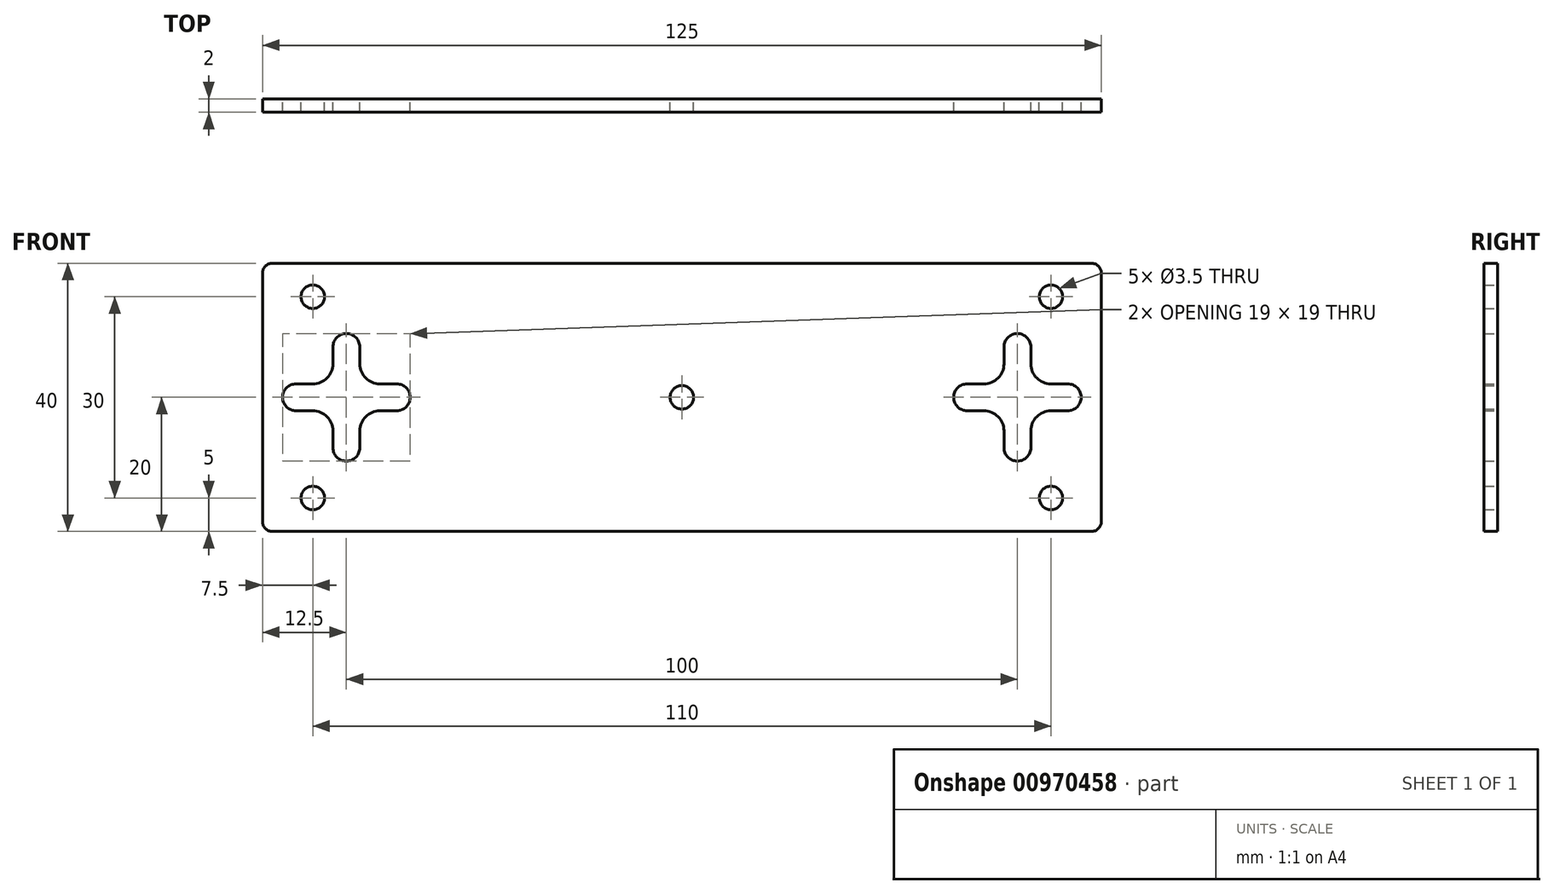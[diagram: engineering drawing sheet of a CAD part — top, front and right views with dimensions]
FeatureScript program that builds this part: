
annotation { "Feature Type Name" : "Feature", "Feature Type Description" : "" }
export const myFeature = defineFeature(function(context is Context, id is Id, definition is map)
    precondition{}
    {
        {
            var Q0;
            Q0=qCreatedBy(makeId("Front.planeOp"),FACE);
            var sketch = newSketch(context, id + "F0", { "sketchPlane" : qUnion([Q0])});
            skLineSegment(sketch, "E0.0", {"start": v(-62.5, 20) * mm, "end": v(62.5, 20) * mm});
            skLineSegment(sketch, "E1.0", {"start": v(-62.5, -20) * mm, "end": v(-62.5, 20) * mm});
            skLineSegment(sketch, "E2.0", {"start": v(-62.5, -20) * mm, "end": v(62.5, -20) * mm});
            skLineSegment(sketch, "E3.0", {"start": v(62.5, -20) * mm, "end": v(62.5, 20) * mm});
            skLineSegment(sketch, "E4.filletArc", {"start": v(-62.5, 20) * mm, "end": v(-62.5, 20) * mm});
            skLineSegment(sketch, "E5.filletArc", {"start": v(-62.5, -20) * mm, "end": v(-62.5, -20) * mm});
            skLineSegment(sketch, "E6.filletArc", {"start": v(62.5, -20) * mm, "end": v(62.5, -20) * mm});
            skLineSegment(sketch, "E7.filletArc", {"start": v(62.5, 20) * mm, "end": v(62.5, 20) * mm});
            skCircle(sketch, "E8", {"center": v(-55, 15) * mm, "radius": 1.75 * mm});
            skCircle(sketch, "E9", {"center": v(55, 15) * mm, "radius": 1.75 * mm});
            skCircle(sketch, "E10", {"center": v(-55, -15) * mm, "radius": 1.75 * mm});
            skCircle(sketch, "E11", {"center": v(55, -15) * mm, "radius": 1.75 * mm});
            skLineSegment(sketch, "E12", {"start": v(-50, 7.5) * mm, "end": v(-50, -7.5) * mm});
            skLineSegment(sketch, "E13", {"start": v(42.5, 0) * mm, "end": v(57.5, 0) * mm});
            skLineSegment(sketch, "E14", {"start": v(50, 7.5) * mm, "end": v(50, -7.5) * mm});
            skLineSegment(sketch, "E15", {"start": v(-57.5, 0) * mm, "end": v(-42.5, 0) * mm});
            skArc(sketch, "E16.0.startCap", {"start": v(48, 7.5) * mm, "mid": v(50, 9.5) * mm, "end": v(52, 7.5) * mm});
            skArc(sketch, "E16.0.endCap", {"start": v(52, -7.5) * mm, "mid": v(50, -9.5) * mm, "end": v(48, -7.5) * mm});
            skLineSegment(sketch, "E16.0.left", {"start": v(52, 7.5) * mm, "end": v(52, -7.5) * mm});
            skLineSegment(sketch, "E16.0.right", {"start": v(48, 7.5) * mm, "end": v(48, -7.5) * mm});
            skArc(sketch, "E17.0.startCap", {"start": v(42.5, -2) * mm, "mid": v(40.5, 0) * mm, "end": v(42.5, 2) * mm});
            skArc(sketch, "E17.0.endCap", {"start": v(57.5, 2) * mm, "mid": v(59.5, 0) * mm, "end": v(57.5, -2) * mm});
            skLineSegment(sketch, "E17.0.left", {"start": v(42.5, 2) * mm, "end": v(57.5, 2) * mm});
            skLineSegment(sketch, "E17.0.right", {"start": v(42.5, -2) * mm, "end": v(57.5, -2) * mm});
            skArc(sketch, "E17.1.startCap", {"start": v(-57.5, -2) * mm, "mid": v(-59.5, 0) * mm, "end": v(-57.5, 2) * mm});
            skArc(sketch, "E17.1.endCap", {"start": v(-42.5, 2) * mm, "mid": v(-40.5, 0) * mm, "end": v(-42.5, -2) * mm});
            skLineSegment(sketch, "E17.1.left", {"start": v(-57.5, 2) * mm, "end": v(-42.5, 2) * mm});
            skLineSegment(sketch, "E17.1.right", {"start": v(-57.5, -2) * mm, "end": v(-42.5, -2) * mm});
            skArc(sketch, "E17.2.startCap", {"start": v(-52, 7.5) * mm, "mid": v(-50, 9.5) * mm, "end": v(-48, 7.5) * mm});
            skArc(sketch, "E17.2.endCap", {"start": v(-48, -7.5) * mm, "mid": v(-50, -9.5) * mm, "end": v(-52, -7.5) * mm});
            skLineSegment(sketch, "E17.2.left", {"start": v(-48, 7.5) * mm, "end": v(-48, -7.5) * mm});
            skLineSegment(sketch, "E17.2.right", {"start": v(-52, 7.5) * mm, "end": v(-52, -7.5) * mm});
            skCircle(sketch, "E18", {"center": v(0, 0) * mm, "radius": 1.75 * mm});
            skSolve(sketch);
        }
        {
            var Q0;
            {var subQ14=sQuery(id+"F0.wireOp",EDGE,"E0.0");Q0=makeQuery(id+"F0.imprint","IMPRINT",FACE,{"disambiguationData":[TD([[makeQuery(id+"F0.imprint","IMPRINT",EDGE,{"derivedFrom":subQ14}),-1.0]])]});}
            var Q1;
            {var subQ10=sQuery(id+"F0.wireOp",EDGE,"E2.0");Q1=makeQuery(id+"F0.imprint","IMPRINT",FACE,{"disambiguationData":[TD([[makeQuery(id+"F0.imprint","IMPRINT",EDGE,{"derivedFrom":subQ10}),1.0]])]});}
            var Q2;
            {var subQ1=sQuery(id+"F0.wireOp",EDGE,"X3yWnhJm-qIiu-0vvX-LXHK-jDvgxX4Z6LWV.bottom");var subQ3=sQuery(id+"F0.wireOp",EDGE,"iid6QfgW-px9S-WGrx-PAUP-FnRUA4cKeCWQ");var subQ4=makeQuery(id+"F0.imprint","INTERSECT",VERTEX,{"derivedFrom":[subQ1,subQ3]});Q2=makeQuery(id+"F0.imprint","IMPRINT",FACE,{"disambiguationData":[TD([[makeQuery(id+"F0.imprint","IMPRINT",EDGE,{"disambiguationData":[TD([[subQ4,-1.0]])],"derivedFrom":subQ3}),-1.0]])]});}
            var Q3;
            {var subQ5=sQuery(id+"F0.wireOp",EDGE,"E10");var subQ6=sQuery(id+"F0.wireOp",EDGE,"X3yWnhJm-qIiu-0vvX-LXHK-jDvgxX4Z6LWV.bottom");var subQ7=makeQuery(id+"F0.imprint","INTERSECT",VERTEX,{"derivedFrom":[subQ6,subQ5]});Q3=makeQuery(id+"F0.imprint","IMPRINT",FACE,{"disambiguationData":[TD([[makeQuery(id+"F0.imprint","IMPRINT",EDGE,{"disambiguationData":[TD([[subQ7,-1.0]])],"derivedFrom":subQ6}),1.0]])]});}
            var Q4;
            {var subQ1=sQuery(id+"F0.wireOp",EDGE,"X3yWnhJm-qIiu-0vvX-LXHK-jDvgxX4Z6LWV.top");var subQ11=sQuery(id+"F0.wireOp",EDGE,"iid6QfgW-px9S-WGrx-PAUP-FnRUA4cKeCWQ");var subQ12=makeQuery(id+"F0.imprint","INTERSECT",VERTEX,{"derivedFrom":[subQ1,subQ11]});Q4=makeQuery(id+"F0.imprint","IMPRINT",FACE,{"disambiguationData":[TD([[makeQuery(id+"F0.imprint","IMPRINT",EDGE,{"disambiguationData":[TD([[subQ12,-1.0]])],"derivedFrom":subQ1}),-1.0]])]});}
            var Q5;
            {var subQ1=sQuery(id+"F0.wireOp",EDGE,"X3yWnhJm-qIiu-0vvX-LXHK-jDvgxX4Z6LWV.top");var subQ3=sQuery(id+"F0.wireOp",EDGE,"iid6QfgW-px9S-WGrx-PAUP-FnRUA4cKeCWQ");var subQ4=makeQuery(id+"F0.imprint","INTERSECT",VERTEX,{"derivedFrom":[subQ1,subQ3]});Q5=makeQuery(id+"F0.imprint","IMPRINT",FACE,{"disambiguationData":[TD([[makeQuery(id+"F0.imprint","IMPRINT",EDGE,{"disambiguationData":[TD([[subQ4,1.0]])],"derivedFrom":subQ3}),1.0]])]});}
            var Q6;
            {var subQ0=sQuery(id+"F0.wireOp",EDGE,"i4QyBCOg-cULm-5afE-RLwa-3CR6AZ6ktZAw");Q6=makeQuery(id+"F0.imprint","IMPRINT",FACE,{"disambiguationData":[TD([[makeQuery(id+"F0.imprint","IMPRINT",EDGE,{"derivedFrom":subQ0}),1.0]])]});}
            var Q7;
            Q7=makeQuery(id+"F0.imprint","IMPRINT",FACE,{"disambiguationData":[TD([[makeQuery(id+"F0.imprint","IMPRINT",EDGE,{"derivedFrom":sQuery(id+"F0.wireOp",EDGE,"mcuOtgL4-kk58-VkkY-zE61-ACZWzzPfrjxR")}),-1.0]])]});
            var Q8;
            {var subQ0=sQuery(id+"F0.wireOp",EDGE,"KWtc0nGb-DVKQ-R7uK-HgXM-ysEQQWN5L63F");var subQ1=sQuery(id+"F0.wireOp",EDGE,"4OTX3qk5-V7Ov-Qq6L-etMf-vckOSsjvSIyS");var subQ2=makeQuery(id+"F0.imprint","INTERSECT",VERTEX,{"derivedFrom":[subQ1,subQ0]});Q8=makeQuery(id+"F0.imprint","IMPRINT",FACE,{"disambiguationData":[TD([[makeQuery(id+"F0.imprint","IMPRINT",EDGE,{"disambiguationData":[TD([[subQ2,-1.0]])],"derivedFrom":subQ1}),-1.0]])]});}
            var Q9;
            {var subQ1=sQuery(id+"F0.wireOp",EDGE,"4OTX3qk5-V7Ov-Qq6L-etMf-vckOSsjvSIyS");var subQ6=sQuery(id+"F0.wireOp",EDGE,"iid6QfgW-px9S-WGrx-PAUP-FnRUA4cKeCWQ");var subQ9=makeQuery(id+"F0.imprint","INTERSECT",VERTEX,{"disambiguationData":[OD(1.0)],"derivedFrom":[subQ6,subQ1]});Q9=makeQuery(id+"F0.imprint","IMPRINT",FACE,{"disambiguationData":[TD([[makeQuery(id+"F0.imprint","IMPRINT",EDGE,{"disambiguationData":[TD([[subQ9,-1.0]])],"derivedFrom":subQ6}),1.0]])]});}
            var Q10;
            {var subQ5=sQuery(id+"F0.wireOp",EDGE,"eCR2NoOr-Eci4-ocfl-Ev2O-bT8fmTrP9O9z");var subQ6=sQuery(id+"F0.wireOp",EDGE,"iid6QfgW-px9S-WGrx-PAUP-FnRUA4cKeCWQ");var subQ7=makeQuery(id+"F0.imprint","INTERSECT",VERTEX,{"disambiguationData":[OD(1.0)],"derivedFrom":[subQ6,subQ5]});Q10=makeQuery(id+"F0.imprint","IMPRINT",FACE,{"disambiguationData":[TD([[makeQuery(id+"F0.imprint","IMPRINT",EDGE,{"disambiguationData":[TD([[subQ7,-1.0]])],"derivedFrom":subQ6}),1.0]])]});}
            var Q11;
            {var subQ0=sQuery(id+"F0.wireOp",EDGE,"KsEaITvz-aWfB-0gTG-2vQc-Dy6UcmHyx8SA");var subQ5=sQuery(id+"F0.wireOp",EDGE,"Y71Hv5pT-VDeY-pl7A-gw0W-9l02TnNV8O4Y");var subQ6=makeQuery(id+"F0.imprint","INTERSECT",VERTEX,{"disambiguationData":[OD(0.0)],"derivedFrom":[subQ0,subQ5]});Q11=makeQuery(id+"F0.imprint","IMPRINT",FACE,{"disambiguationData":[TD([[makeQuery(id+"F0.imprint","IMPRINT",EDGE,{"disambiguationData":[TD([[subQ6,-1.0]])],"derivedFrom":subQ0}),-1.0]])]});}
            var Q12;
            {var subQ0=sQuery(id+"F0.wireOp",EDGE,"eCR2NoOr-Eci4-ocfl-Ev2O-bT8fmTrP9O9z");var subQ1=sQuery(id+"F0.wireOp",EDGE,"iAqB02pa-lLI2-8K0O-0Iya-2bA1iniOnDgh");var subQ2=makeQuery(id+"F0.imprint","INTERSECT",VERTEX,{"disambiguationData":[OD(0.0)],"derivedFrom":[subQ1,subQ0]});Q12=makeQuery(id+"F0.imprint","IMPRINT",FACE,{"disambiguationData":[TD([[makeQuery(id+"F0.imprint","IMPRINT",EDGE,{"disambiguationData":[TD([[subQ2,-1.0]])],"derivedFrom":subQ1}),-1.0]])]});}
            var Q13;
            {var subQ0=sQuery(id+"F0.wireOp",EDGE,"eCR2NoOr-Eci4-ocfl-Ev2O-bT8fmTrP9O9z");var subQ1=sQuery(id+"F0.wireOp",EDGE,"iAqB02pa-lLI2-8K0O-0Iya-2bA1iniOnDgh");var subQ2=makeQuery(id+"F0.imprint","INTERSECT",VERTEX,{"disambiguationData":[OD(0.0)],"derivedFrom":[subQ1,subQ0]});Q13=makeQuery(id+"F0.imprint","IMPRINT",FACE,{"disambiguationData":[TD([[makeQuery(id+"F0.imprint","IMPRINT",EDGE,{"disambiguationData":[TD([[subQ2,-1.0]])],"derivedFrom":subQ1}),1.0]])]});}
            var Q14;
            {var subQ1=sQuery(id+"F0.wireOp",EDGE,"iid6QfgW-px9S-WGrx-PAUP-FnRUA4cKeCWQ");var subQ6=sQuery(id+"F0.wireOp",EDGE,"xezjStJQ-Z63Z-E7xO-FFxy-wJp8TU6c4T7D");var subQ9=makeQuery(id+"F0.imprint","INTERSECT",VERTEX,{"disambiguationData":[OD(0.0)],"derivedFrom":[subQ1,subQ6]});Q14=makeQuery(id+"F0.imprint","IMPRINT",FACE,{"disambiguationData":[TD([[makeQuery(id+"F0.imprint","IMPRINT",EDGE,{"disambiguationData":[TD([[subQ9,-1.0]])],"derivedFrom":subQ1}),-1.0]])]});}
            var Q15;
            {var subQ0=sQuery(id+"F0.wireOp",EDGE,"eCR2NoOr-Eci4-ocfl-Ev2O-bT8fmTrP9O9z");var subQ5=sQuery(id+"F0.wireOp",EDGE,"Y71Hv5pT-VDeY-pl7A-gw0W-9l02TnNV8O4Y");var subQ6=makeQuery(id+"F0.imprint","INTERSECT",VERTEX,{"disambiguationData":[OD(1.0)],"derivedFrom":[subQ0,subQ5]});Q15=makeQuery(id+"F0.imprint","IMPRINT",FACE,{"disambiguationData":[TD([[makeQuery(id+"F0.imprint","IMPRINT",EDGE,{"disambiguationData":[TD([[subQ6,-1.0]])],"derivedFrom":subQ0}),-1.0]])]});}
            var Q16;
            {var subQ0=sQuery(id+"F0.wireOp",EDGE,"hLMzJQcc-tioY-p3Ux-ii9U-QVrMqoF1n24R");var subQ1=sQuery(id+"F0.wireOp",EDGE,"4OTX3qk5-V7Ov-Qq6L-etMf-vckOSsjvSIyS");var subQ2=makeQuery(id+"F0.imprint","INTERSECT",VERTEX,{"derivedFrom":[subQ1,subQ0]});Q16=makeQuery(id+"F0.imprint","IMPRINT",FACE,{"disambiguationData":[TD([[makeQuery(id+"F0.imprint","IMPRINT",EDGE,{"disambiguationData":[TD([[subQ2,-1.0]])],"derivedFrom":subQ1}),-1.0]])]});}
            var Q17;
            {var subQ5=sQuery(id+"F0.wireOp",EDGE,"KsEaITvz-aWfB-0gTG-2vQc-Dy6UcmHyx8SA");var subQ6=sQuery(id+"F0.wireOp",EDGE,"iid6QfgW-px9S-WGrx-PAUP-FnRUA4cKeCWQ");var subQ7=makeQuery(id+"F0.imprint","INTERSECT",VERTEX,{"disambiguationData":[OD(1.0)],"derivedFrom":[subQ6,subQ5]});Q17=makeQuery(id+"F0.imprint","IMPRINT",FACE,{"disambiguationData":[TD([[makeQuery(id+"F0.imprint","IMPRINT",EDGE,{"disambiguationData":[TD([[subQ7,-1.0]])],"derivedFrom":subQ6}),-1.0]])]});}
            var Q18;
            {var subQ0=sQuery(id+"F0.wireOp",EDGE,"4OTX3qk5-V7Ov-Qq6L-etMf-vckOSsjvSIyS");var subQ1=sQuery(id+"F0.wireOp",EDGE,"iid6QfgW-px9S-WGrx-PAUP-FnRUA4cKeCWQ");var subQ2=makeQuery(id+"F0.imprint","INTERSECT",VERTEX,{"disambiguationData":[OD(0.0)],"derivedFrom":[subQ1,subQ0]});Q18=makeQuery(id+"F0.imprint","IMPRINT",FACE,{"disambiguationData":[TD([[makeQuery(id+"F0.imprint","IMPRINT",EDGE,{"disambiguationData":[TD([[subQ2,-1.0]])],"derivedFrom":subQ1}),-1.0]])]});}
            var Q19;
            {var subQ0=sQuery(id+"F0.wireOp",EDGE,"hLMzJQcc-tioY-p3Ux-ii9U-QVrMqoF1n24R");var subQ1=sQuery(id+"F0.wireOp",EDGE,"4OTX3qk5-V7Ov-Qq6L-etMf-vckOSsjvSIyS");var subQ2=makeQuery(id+"F0.imprint","INTERSECT",VERTEX,{"derivedFrom":[subQ1,subQ0]});Q19=makeQuery(id+"F0.imprint","IMPRINT",FACE,{"disambiguationData":[TD([[makeQuery(id+"F0.imprint","IMPRINT",EDGE,{"disambiguationData":[TD([[subQ2,1.0]])],"derivedFrom":subQ0}),1.0]])]});}
            var Q20;
            {var subQ0=sQuery(id+"F0.wireOp",EDGE,"mETCbggD-oOKK-MaU9-OdIb-20X2RE9a2U7w");var subQ1=sQuery(id+"F0.wireOp",EDGE,"iid6QfgW-px9S-WGrx-PAUP-FnRUA4cKeCWQ");var subQ2=makeQuery(id+"F0.imprint","INTERSECT",VERTEX,{"disambiguationData":[OD(1.0)],"derivedFrom":[subQ1,subQ0]});Q20=makeQuery(id+"F0.imprint","IMPRINT",FACE,{"disambiguationData":[TD([[makeQuery(id+"F0.imprint","IMPRINT",EDGE,{"disambiguationData":[TD([[subQ2,-1.0]])],"derivedFrom":subQ1}),-1.0]])]});}
            var Q21;
            {var subQ0=sQuery(id+"F0.wireOp",EDGE,"mETCbggD-oOKK-MaU9-OdIb-20X2RE9a2U7w");var subQ1=sQuery(id+"F0.wireOp",EDGE,"iid6QfgW-px9S-WGrx-PAUP-FnRUA4cKeCWQ");var subQ2=makeQuery(id+"F0.imprint","INTERSECT",VERTEX,{"disambiguationData":[OD(1.0)],"derivedFrom":[subQ1,subQ0]});Q21=makeQuery(id+"F0.imprint","IMPRINT",FACE,{"disambiguationData":[TD([[makeQuery(id+"F0.imprint","IMPRINT",EDGE,{"disambiguationData":[TD([[subQ2,-1.0]])],"derivedFrom":subQ1}),1.0]])]});}
            var Q22;
            {var subQ0=sQuery(id+"F0.wireOp",EDGE,"KWtc0nGb-DVKQ-R7uK-HgXM-ysEQQWN5L63F");var subQ1=sQuery(id+"F0.wireOp",EDGE,"4OTX3qk5-V7Ov-Qq6L-etMf-vckOSsjvSIyS");var subQ2=makeQuery(id+"F0.imprint","INTERSECT",VERTEX,{"derivedFrom":[subQ1,subQ0]});Q22=makeQuery(id+"F0.imprint","IMPRINT",FACE,{"disambiguationData":[TD([[makeQuery(id+"F0.imprint","IMPRINT",EDGE,{"disambiguationData":[TD([[subQ2,1.0]])],"derivedFrom":subQ0}),1.0]])]});}
            var Q23;
            {var subQ0=sQuery(id+"F0.wireOp",EDGE,"4OTX3qk5-V7Ov-Qq6L-etMf-vckOSsjvSIyS");var subQ1=sQuery(id+"F0.wireOp",EDGE,"iid6QfgW-px9S-WGrx-PAUP-FnRUA4cKeCWQ");var subQ2=makeQuery(id+"F0.imprint","INTERSECT",VERTEX,{"disambiguationData":[OD(0.0)],"derivedFrom":[subQ1,subQ0]});Q23=makeQuery(id+"F0.imprint","IMPRINT",FACE,{"disambiguationData":[TD([[makeQuery(id+"F0.imprint","IMPRINT",EDGE,{"disambiguationData":[TD([[subQ2,-1.0]])],"derivedFrom":subQ1}),1.0]])]});}
            var Q24;
            {var subQ0=sQuery(id+"F0.wireOp",EDGE,"KsEaITvz-aWfB-0gTG-2vQc-Dy6UcmHyx8SA");var subQ1=sQuery(id+"F0.wireOp",EDGE,"iAqB02pa-lLI2-8K0O-0Iya-2bA1iniOnDgh");var subQ2=makeQuery(id+"F0.imprint","INTERSECT",VERTEX,{"disambiguationData":[OD(1.0)],"derivedFrom":[subQ1,subQ0]});Q24=makeQuery(id+"F0.imprint","IMPRINT",FACE,{"disambiguationData":[TD([[makeQuery(id+"F0.imprint","IMPRINT",EDGE,{"disambiguationData":[TD([[subQ2,-1.0]])],"derivedFrom":subQ1}),1.0]])]});}
            var Q25;
            {var subQ0=sQuery(id+"F0.wireOp",EDGE,"KsEaITvz-aWfB-0gTG-2vQc-Dy6UcmHyx8SA");var subQ1=sQuery(id+"F0.wireOp",EDGE,"iAqB02pa-lLI2-8K0O-0Iya-2bA1iniOnDgh");var subQ2=makeQuery(id+"F0.imprint","INTERSECT",VERTEX,{"disambiguationData":[OD(1.0)],"derivedFrom":[subQ1,subQ0]});Q25=makeQuery(id+"F0.imprint","IMPRINT",FACE,{"disambiguationData":[TD([[makeQuery(id+"F0.imprint","IMPRINT",EDGE,{"disambiguationData":[TD([[subQ2,-1.0]])],"derivedFrom":subQ1}),-1.0]])]});}
            var Q26;
            {var subQ0=sQuery(id+"F0.wireOp",EDGE,"xezjStJQ-Z63Z-E7xO-FFxy-wJp8TU6c4T7D");var subQ1=sQuery(id+"F0.wireOp",EDGE,"iid6QfgW-px9S-WGrx-PAUP-FnRUA4cKeCWQ");var subQ2=makeQuery(id+"F0.imprint","INTERSECT",VERTEX,{"disambiguationData":[OD(0.0)],"derivedFrom":[subQ1,subQ0]});Q26=makeQuery(id+"F0.imprint","IMPRINT",FACE,{"disambiguationData":[TD([[makeQuery(id+"F0.imprint","IMPRINT",EDGE,{"disambiguationData":[TD([[subQ2,-1.0]])],"derivedFrom":subQ1}),1.0]])]});}
            var Q27;
            {var subQ0=sQuery(id+"F0.wireOp",EDGE,"KsEaITvz-aWfB-0gTG-2vQc-Dy6UcmHyx8SA");var subQ1=sQuery(id+"F0.wireOp",EDGE,"iid6QfgW-px9S-WGrx-PAUP-FnRUA4cKeCWQ");var subQ2=makeQuery(id+"F0.imprint","INTERSECT",VERTEX,{"disambiguationData":[OD(1.0)],"derivedFrom":[subQ1,subQ0]});Q27=makeQuery(id+"F0.imprint","IMPRINT",FACE,{"disambiguationData":[TD([[makeQuery(id+"F0.imprint","IMPRINT",EDGE,{"disambiguationData":[TD([[subQ2,-1.0]])],"derivedFrom":subQ1}),1.0]])]});}
            var Q28;
            {var subQ0=sQuery(id+"F0.wireOp",EDGE,"4OTX3qk5-V7Ov-Qq6L-etMf-vckOSsjvSIyS");var subQ1=sQuery(id+"F0.wireOp",EDGE,"iid6QfgW-px9S-WGrx-PAUP-FnRUA4cKeCWQ");var subQ2=makeQuery(id+"F0.imprint","INTERSECT",VERTEX,{"disambiguationData":[OD(1.0)],"derivedFrom":[subQ1,subQ0]});Q28=makeQuery(id+"F0.imprint","IMPRINT",FACE,{"disambiguationData":[TD([[makeQuery(id+"F0.imprint","IMPRINT",EDGE,{"disambiguationData":[TD([[subQ2,-1.0]])],"derivedFrom":subQ1}),-1.0]])]});}
            var Q29;
            {var subQ0=sQuery(id+"F0.wireOp",EDGE,"eCR2NoOr-Eci4-ocfl-Ev2O-bT8fmTrP9O9z");var subQ1=sQuery(id+"F0.wireOp",EDGE,"iid6QfgW-px9S-WGrx-PAUP-FnRUA4cKeCWQ");var subQ2=makeQuery(id+"F0.imprint","INTERSECT",VERTEX,{"disambiguationData":[OD(1.0)],"derivedFrom":[subQ1,subQ0]});Q29=makeQuery(id+"F0.imprint","IMPRINT",FACE,{"disambiguationData":[TD([[makeQuery(id+"F0.imprint","IMPRINT",EDGE,{"disambiguationData":[TD([[subQ2,-1.0]])],"derivedFrom":subQ1}),-1.0]])]});}
            extrude(context, id + "F1", {"entities" : qUnion([Q0, Q1, Q2, Q3, Q4, Q5, Q6, Q7, Q8, Q9, Q10, Q11, Q12, Q13, Q14, Q15, Q16, Q17, Q18, Q19, Q20, Q21, Q22, Q23, Q24, Q25, Q26, Q27, Q28, Q29]), "depth" : 2 * mm, "offsetDistance" : 25 * mm});
        }
        {
            var Q0;
            Q0=makeQuery(id+"F1.opExtrude","SWEPT_EDGE",EDGE,{"disambiguationData":[OSD([sQuery(id+"F0.wireOp",EDGE,"E0.0"),sQuery(id+"F0.wireOp",EDGE,"E1.0")])]});
            var Q1;
            Q1=makeQuery(id+"F1.opExtrude","SWEPT_EDGE",EDGE,{"disambiguationData":[OSD([sQuery(id+"F0.wireOp",EDGE,"E0.0"),sQuery(id+"F0.wireOp",EDGE,"E3.0"),sQuery(id+"F0.wireOp",EDGE,"iid6QfgW-px9S-WGrx-PAUP-FnRUA4cKeCWQ")])]});
            var Q2;
            Q2=makeQuery(id+"F1.opExtrude","SWEPT_EDGE",EDGE,{"disambiguationData":[OSD([sQuery(id+"F0.wireOp",EDGE,"E1.0"),sQuery(id+"F0.wireOp",EDGE,"E2.0"),sQuery(id+"F0.wireOp",EDGE,"iid6QfgW-px9S-WGrx-PAUP-FnRUA4cKeCWQ")])]});
            var Q3;
            Q3=makeQuery(id+"F1.opExtrude","SWEPT_EDGE",EDGE,{"disambiguationData":[OSD([sQuery(id+"F0.wireOp",EDGE,"E2.0"),sQuery(id+"F0.wireOp",EDGE,"E3.0")])]});
            fillet(context, id + "F2", {"entities" : qUnion([Q0, Q1, Q2, Q3]), "radius" : 1.5 * mm, "tangentPropagation" : true, "allowEdgeOverflow" : false});
        }
        {
            var Q0;
            Q0=makeQuery(id+"F1.opExtrude","SWEPT_EDGE",EDGE,{"disambiguationData":[OSD([sQuery(id+"F0.wireOp",EDGE,"E17.1.left"),sQuery(id+"F0.wireOp",EDGE,"E17.2.left")])]});
            var Q1;
            Q1=makeQuery(id+"F1.opExtrude","SWEPT_EDGE",EDGE,{"disambiguationData":[OSD([sQuery(id+"F0.wireOp",EDGE,"E17.1.left"),sQuery(id+"F0.wireOp",EDGE,"E17.2.right")])]});
            var Q2;
            Q2=makeQuery(id+"F1.opExtrude","SWEPT_EDGE",EDGE,{"disambiguationData":[OSD([sQuery(id+"F0.wireOp",EDGE,"E17.1.right"),sQuery(id+"F0.wireOp",EDGE,"E17.2.right")])]});
            var Q3;
            Q3=makeQuery(id+"F1.opExtrude","SWEPT_EDGE",EDGE,{"disambiguationData":[OSD([sQuery(id+"F0.wireOp",EDGE,"E17.1.right"),sQuery(id+"F0.wireOp",EDGE,"E17.2.left")])]});
            var Q4;
            Q4=makeQuery(id+"F1.opExtrude","SWEPT_EDGE",EDGE,{"disambiguationData":[OSD([sQuery(id+"F0.wireOp",EDGE,"E16.0.left"),sQuery(id+"F0.wireOp",EDGE,"E17.0.left")])]});
            var Q5;
            Q5=makeQuery(id+"F1.opExtrude","SWEPT_EDGE",EDGE,{"disambiguationData":[OSD([sQuery(id+"F0.wireOp",EDGE,"E16.0.right"),sQuery(id+"F0.wireOp",EDGE,"E17.0.left")])]});
            var Q6;
            Q6=makeQuery(id+"F1.opExtrude","SWEPT_EDGE",EDGE,{"disambiguationData":[OSD([sQuery(id+"F0.wireOp",EDGE,"E16.0.right"),sQuery(id+"F0.wireOp",EDGE,"E17.0.right")])]});
            var Q7;
            Q7=makeQuery(id+"F1.opExtrude","SWEPT_EDGE",EDGE,{"disambiguationData":[OSD([sQuery(id+"F0.wireOp",EDGE,"E16.0.left"),sQuery(id+"F0.wireOp",EDGE,"E17.0.right")])]});
            fillet(context, id + "F3", {"entities" : qUnion([Q0, Q1, Q2, Q3, Q4, Q5, Q6, Q7]), "radius" : 3 * mm, "tangentPropagation" : true, "allowEdgeOverflow" : false});
        }
    });
